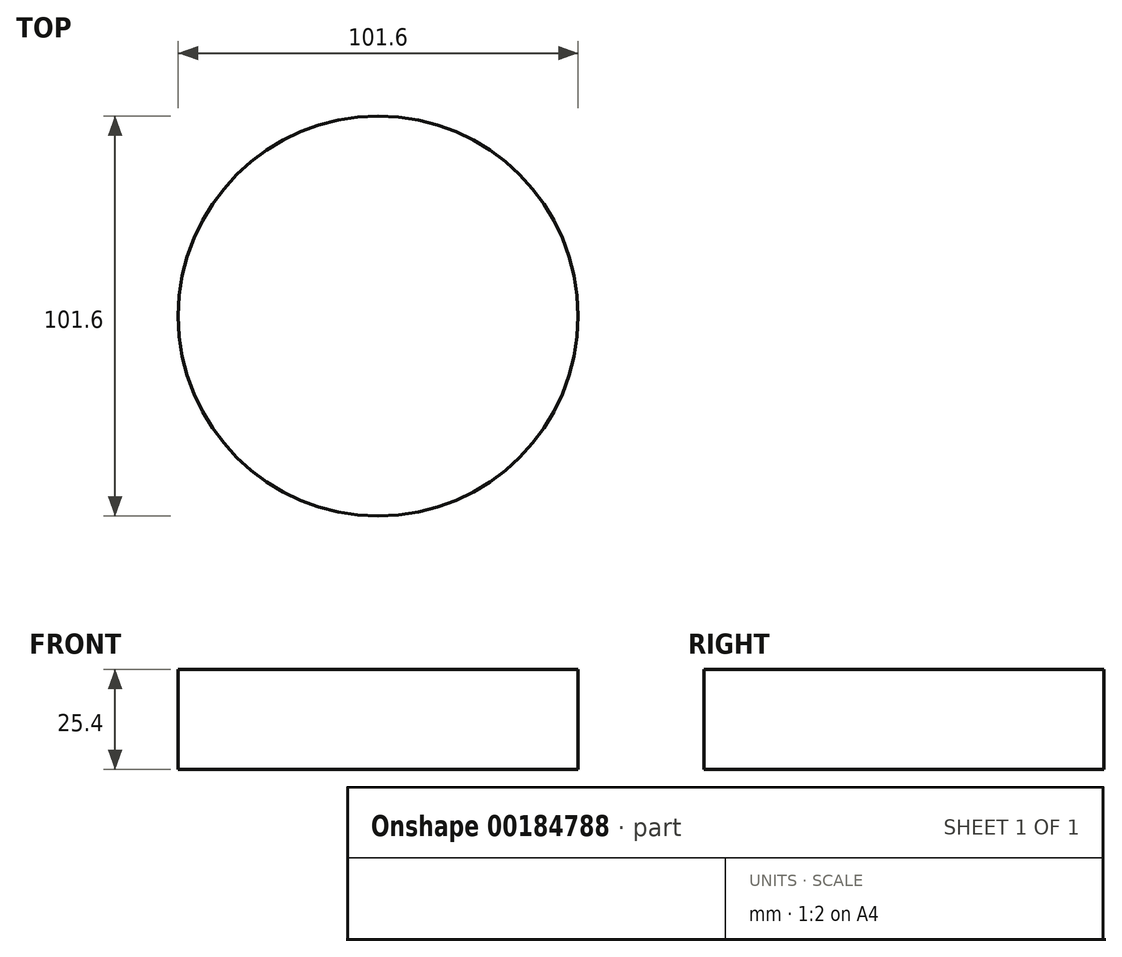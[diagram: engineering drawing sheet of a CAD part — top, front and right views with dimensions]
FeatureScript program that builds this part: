
annotation { "Feature Type Name" : "Feature", "Feature Type Description" : "" }
export const myFeature = defineFeature(function(context is Context, id is Id, definition is map)
    precondition{}
    {
        {
            var Q0;
            Q0=qCreatedBy(makeId("Top.planeOp"),FACE);
            var sketch = newSketch(context, id + "F0", { "sketchPlane" : qUnion([Q0])});
            skCircle(sketch, "E0", {"center": v(0, 0) * mm, "radius": 50.8 * mm});
            skSolve(sketch);
        }
        {
            var Q0;
            Q0=qSketchRegion(id+"F0",true);
            extrude(context, id + "F1", {"entities" : qUnion([Q0]), "depth" : 25.4 * mm});
        }
    });
